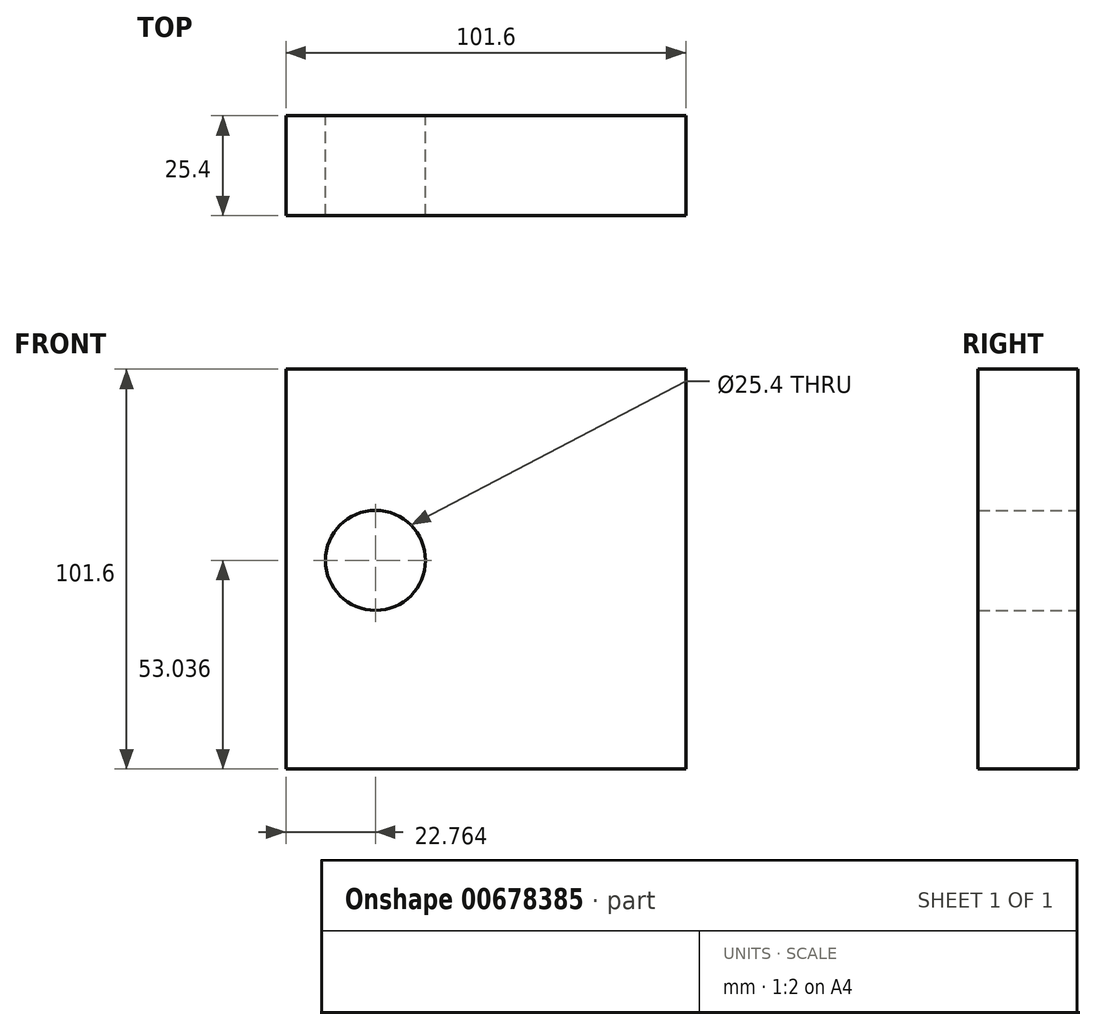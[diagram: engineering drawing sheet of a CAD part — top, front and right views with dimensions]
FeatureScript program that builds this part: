
annotation { "Feature Type Name" : "Feature", "Feature Type Description" : "" }
export const myFeature = defineFeature(function(context is Context, id is Id, definition is map)
    precondition{}
    {
        {
            var Q0;
            Q0=qCreatedBy(makeId("Front.planeOp"),FACE);
            var sketch = newSketch(context, id + "F0", { "sketchPlane" : qUnion([Q0])});
            skCircle(sketch, "E0", {"center": v(-50.38, 61.13) * mm, "radius": 12.7 * mm});
            skLineSegment(sketch, "E1.bottom", {"start": v(-73.14, 109.7) * mm, "end": v(28.46, 109.7) * mm});
            skLineSegment(sketch, "E1.top", {"start": v(-73.14, 8.1) * mm, "end": v(28.46, 8.1) * mm});
            skLineSegment(sketch, "E1.left", {"start": v(-73.14, 109.7) * mm, "end": v(-73.14, 8.1) * mm});
            skLineSegment(sketch, "E1.right", {"start": v(28.46, 109.7) * mm, "end": v(28.46, 8.1) * mm});
            skSolve(sketch);
        }
        {
            var Q0;
            Q0 = qSketchRegion(id + "F0", true);
            extrude(context, id + "F1", {"entities" : qUnion([Q0]), "depth" : 25.4 * mm, "offsetDistance" : 25.4 * mm});
        }
    });
